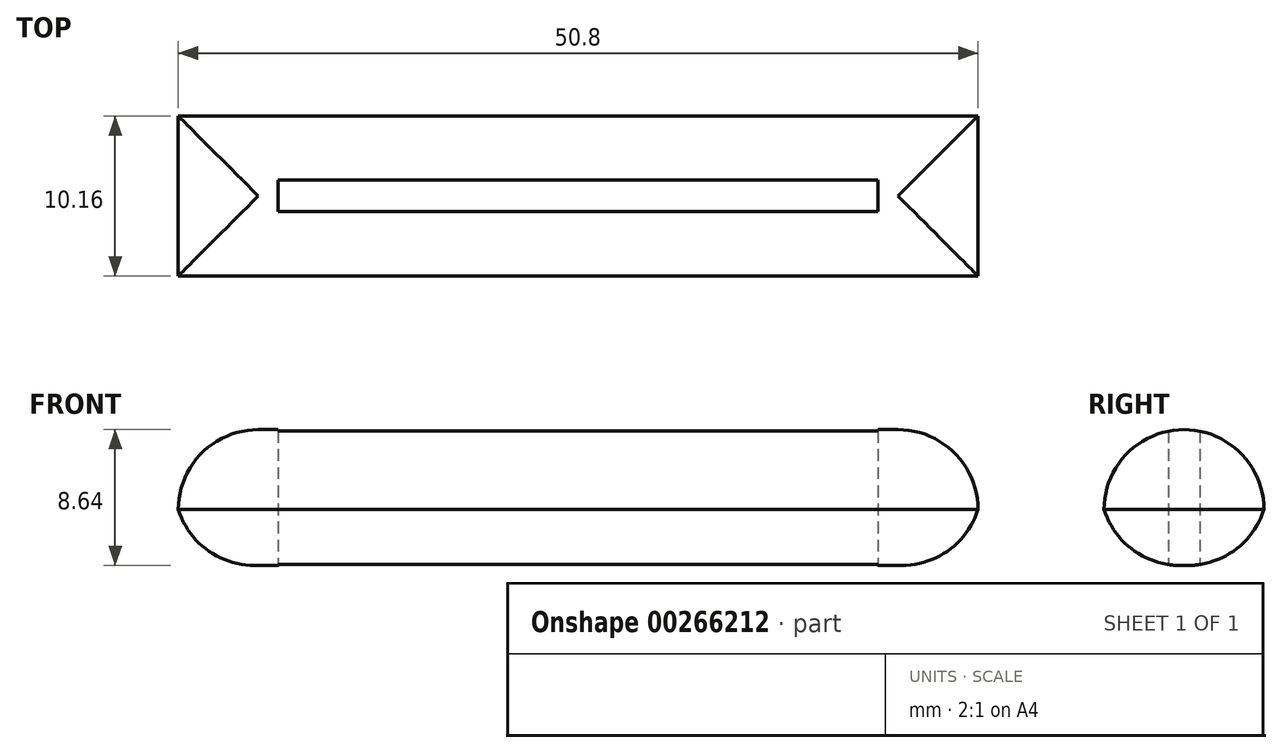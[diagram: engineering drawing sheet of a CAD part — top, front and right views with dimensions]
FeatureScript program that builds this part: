
annotation { "Feature Type Name" : "Feature", "Feature Type Description" : "" }
export const myFeature = defineFeature(function(context is Context, id is Id, definition is map)
    precondition{}
    {
        {
            var Q0;
            Q0=qCreatedBy(makeId("Top.planeOp"),FACE);
            var sketch = newSketch(context, id + "F0", { "sketchPlane" : qUnion([Q0])});
            skLineSegment(sketch, "E0.bottom", {"start": v(19.05, -1) * mm, "end": v(-19.05, -1) * mm});
            skLineSegment(sketch, "E0.top", {"start": v(19.05, 1) * mm, "end": v(-19.05, 1) * mm});
            skLineSegment(sketch, "E0.left", {"start": v(19.05, -1) * mm, "end": v(19.05, 1) * mm});
            skLineSegment(sketch, "E0.right", {"start": v(-19.05, -1) * mm, "end": v(-19.05, 1) * mm});
            skPoint(sketch, "E0.middle", {"position": v(0, 0) * mm});
            skLineSegment(sketch, "E1.bottom", {"start": v(25.4, -5.08) * mm, "end": v(-25.4, -5.08) * mm});
            skLineSegment(sketch, "E1.top", {"start": v(25.4, 5.08) * mm, "end": v(-25.4, 5.08) * mm});
            skLineSegment(sketch, "E1.left", {"start": v(25.4, -5.08) * mm, "end": v(25.4, 5.08) * mm});
            skLineSegment(sketch, "E1.right", {"start": v(-25.4, -5.08) * mm, "end": v(-25.4, 5.08) * mm});
            skSolve(sketch);
        }
        {
            var Q0;
            Q0=makeQuery(id+"F0.imprint","IMPRINT",FACE,{"disambiguationData":[TD([[makeQuery(id+"F0.imprint","IMPRINT",EDGE,{"derivedFrom":sQuery(id+"F0.wireOp",EDGE,"E0.bottom")}),1.0]])]});
            extrude(context, id + "F1", {"entities" : qUnion([Q0]), "depth" : 8.64 * mm});
        }
        {
            var Q0;
            Q0=makeQuery(id+"F1.opExtrude","CAP_EDGE",EDGE,{"disambiguationData":[OSD([sQuery(id+"F0.wireOp",EDGE,"E1.right")])],"isStart":false});
            var Q1;
            Q1=makeQuery(id+"F1.opExtrude","CAP_EDGE",EDGE,{"disambiguationData":[OSD([sQuery(id+"F0.wireOp",EDGE,"E1.bottom")])],"isStart":false});
            var Q2;
            Q2=makeQuery(id+"F1.opExtrude","CAP_EDGE",EDGE,{"disambiguationData":[OSD([sQuery(id+"F0.wireOp",EDGE,"E1.left")])],"isStart":false});
            var Q3;
            Q3=makeQuery(id+"F1.opExtrude","CAP_EDGE",EDGE,{"disambiguationData":[OSD([sQuery(id+"F0.wireOp",EDGE,"E1.top")])],"isStart":false});
            fillet(context, id + "F2", {"entities" : qUnion([Q0, Q1, Q2, Q3]), "radius" : 5.08 * mm, "tangentPropagation" : true, "allowEdgeOverflow" : false});
        }
        {
            var Q0;
            Q0=makeQuery(id+"F1.opExtrude","CAP_EDGE",EDGE,{"disambiguationData":[OSD([sQuery(id+"F0.wireOp",EDGE,"E1.right")])],"isStart":true});
            var Q1;
            Q1=makeQuery(id+"F1.opExtrude","CAP_EDGE",EDGE,{"disambiguationData":[OSD([sQuery(id+"F0.wireOp",EDGE,"E1.bottom")])],"isStart":true});
            var Q2;
            Q2=makeQuery(id+"F1.opExtrude","CAP_EDGE",EDGE,{"disambiguationData":[OSD([sQuery(id+"F0.wireOp",EDGE,"E1.top")])],"isStart":true});
            var Q3;
            Q3=makeQuery(id+"F1.opExtrude","CAP_EDGE",EDGE,{"disambiguationData":[OSD([sQuery(id+"F0.wireOp",EDGE,"E1.left")])],"isStart":true});
            fillet(context, id + "F3", {"entities" : qUnion([Q0, Q1, Q2, Q3]), "radius" : 5.08 * mm, "tangentPropagation" : true, "allowEdgeOverflow" : false});
        }
    });
